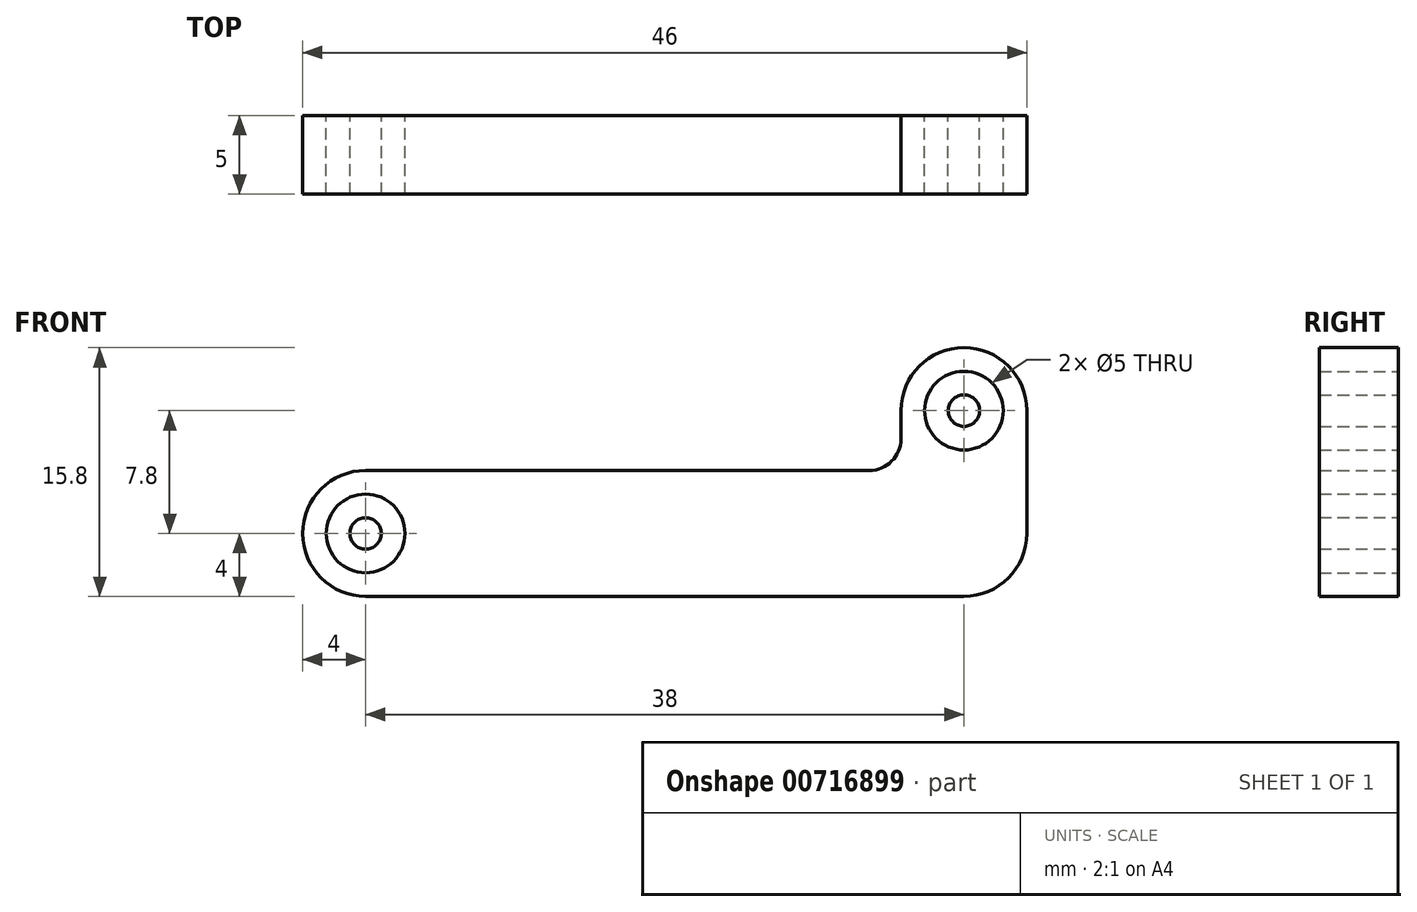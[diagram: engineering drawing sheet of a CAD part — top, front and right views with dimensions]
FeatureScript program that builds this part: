
annotation { "Feature Type Name" : "Feature", "Feature Type Description" : "" }
export const myFeature = defineFeature(function(context is Context, id is Id, definition is map)
    precondition{}
    {
        {
            var Q0;
            Q0=qCreatedBy(makeId("Front.planeOp"),FACE);
            var sketch = newSketch(context, id + "F0", { "sketchPlane" : qUnion([Q0])});
            skArc(sketch, "E0", {"start": v(0, 4) * mm, "mid": v(-4, 0) * mm, "end": v(0, -4) * mm});
            skArc(sketch, "E1", {"start": v(42, 7.8) * mm, "mid": v(38, 11.8) * mm, "end": v(34, 7.8) * mm});
            skLineSegment(sketch, "E2", {"start": v(0, -4) * mm, "end": v(38, -4) * mm});
            skLineSegment(sketch, "E3", {"start": v(42, 0) * mm, "end": v(42, 7.8) * mm});
            skLineSegment(sketch, "E4", {"start": v(34, 7.8) * mm, "end": v(34, 6) * mm});
            skLineSegment(sketch, "E5", {"start": v(32, 4) * mm, "end": v(0, 4) * mm});
            skPoint(sketch, "E6.visualSharp", {"position": v(42, -4) * mm});
            skArc(sketch, "E6.filletArc", {"start": v(38, -4) * mm, "mid": v(40.83, -2.83) * mm, "end": v(42, 0) * mm});
            skPoint(sketch, "E7.visualSharp", {"position": v(34, 4) * mm});
            skArc(sketch, "E7.filletArc", {"start": v(32, 4) * mm, "mid": v(33.41, 4.59) * mm, "end": v(34, 6) * mm});
            skCircle(sketch, "E8", {"center": v(0, 0) * mm, "radius": 2.5 * mm});
            skCircle(sketch, "E9", {"center": v(38, 7.8) * mm, "radius": 2.5 * mm});
            skCircle(sketch, "E10", {"center": v(38, 7.8) * mm, "radius": 1 * mm});
            skCircle(sketch, "E11", {"center": v(0, 0) * mm, "radius": 1 * mm});
            skSolve(sketch);
        }
        {
            var Q0;
            Q0 = qSketchRegion(id + "F0", true);
            var Q1;
            Q1=makeQuery(id+"F0.imprint","IMPRINT",FACE,{"disambiguationData":[TD([[makeQuery(id+"F0.imprint","IMPRINT",EDGE,{"derivedFrom":sQuery(id+"F0.wireOp",EDGE,"E11")}),1.0]])]});
            var Q2;
            Q2=makeQuery(id+"F0.imprint","IMPRINT",FACE,{"disambiguationData":[TD([[makeQuery(id+"F0.imprint","IMPRINT",EDGE,{"derivedFrom":sQuery(id+"F0.wireOp",EDGE,"E10")}),1.0]])]});
            extrude(context, id + "F1", {"entities" : qUnion([Q0, Q1, Q2]), "depth" : 5 * mm, "offsetDistance" : 25.4 * mm});
        }
    });
